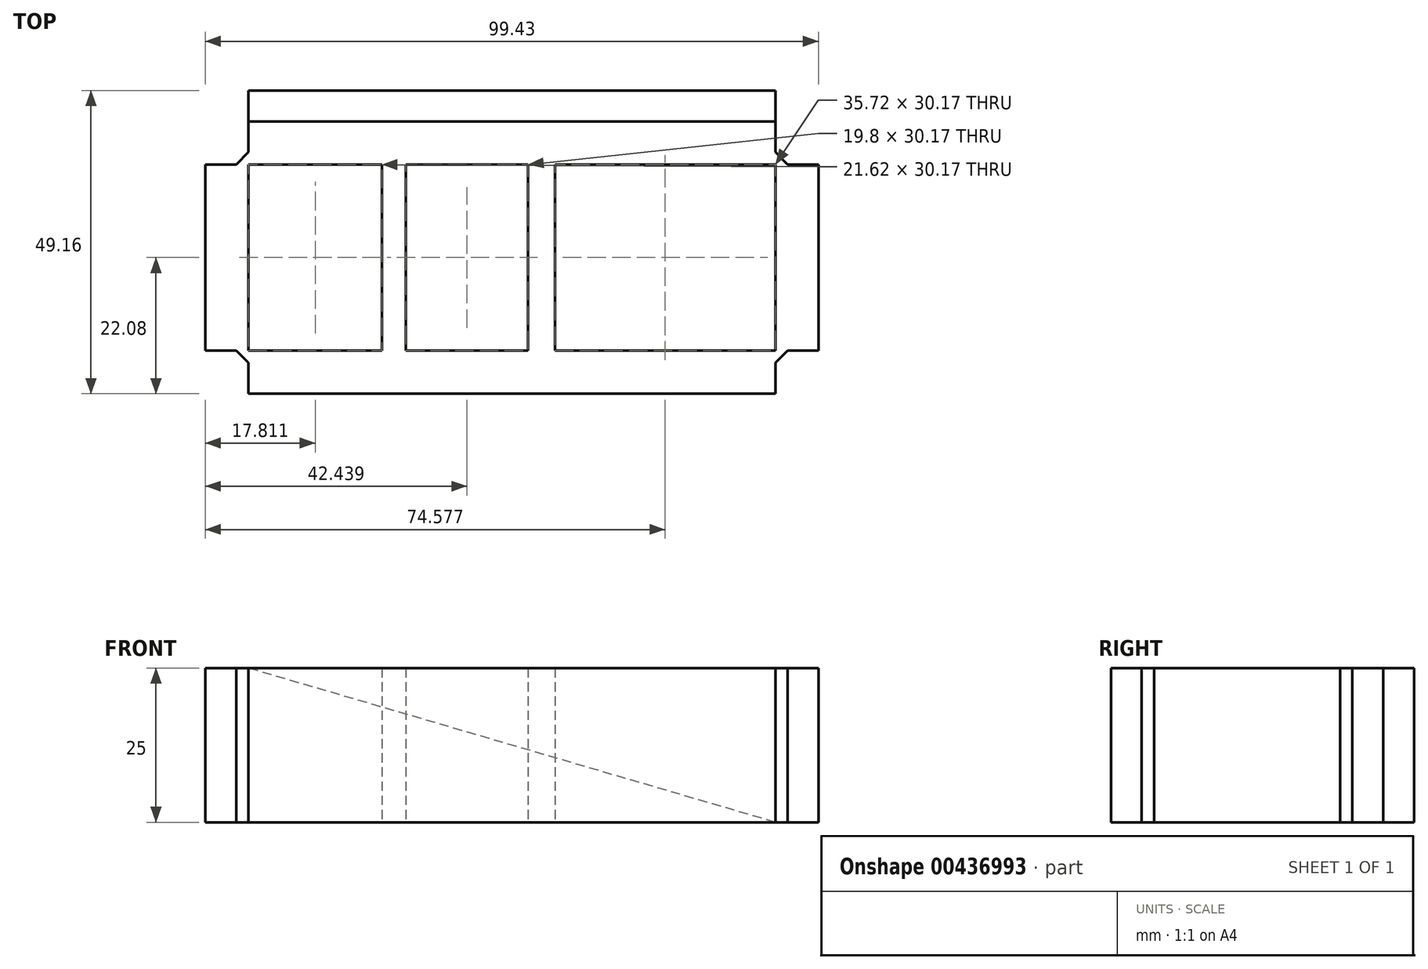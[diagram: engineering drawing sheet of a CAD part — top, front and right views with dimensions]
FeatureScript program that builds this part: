
annotation { "Feature Type Name" : "Feature", "Feature Type Description" : "" }
export const myFeature = defineFeature(function(context is Context, id is Id, definition is map)
    precondition{}
    {
        {
            var Q0;
            Q0=qCreatedBy(makeId("Top.planeOp"),FACE);
            var sketch = newSketch(context, id + "F0", { "sketchPlane" : qUnion([Q0])});
            skLineSegment(sketch, "E0.left", {"start": v(-36.76, 13.37) * mm, "end": v(-36.76, -16.8) * mm});
            skLineSegment(sketch, "E0.right", {"start": v(48.67, 13.37) * mm, "end": v(48.67, -16.8) * mm});
            skLineSegment(sketch, "E1.0", {"start": v(-38.76, 13.37) * mm, "end": v(-38.76, -16.8) * mm});
            skLineSegment(sketch, "E2.0", {"start": v(-36.76, 15.37) * mm, "end": v(48.67, 15.37) * mm});
            skLineSegment(sketch, "E3.0", {"start": v(50.67, 13.37) * mm, "end": v(50.67, -16.8) * mm});
            skLineSegment(sketch, "E4.0", {"start": v(-36.76, -18.8) * mm, "end": v(48.67, -18.8) * mm});
            skLineSegment(sketch, "E5", {"start": v(-36.76, 15.37) * mm, "end": v(-38.76, 13.37) * mm});
            skLineSegment(sketch, "E6", {"start": v(48.67, 15.37) * mm, "end": v(50.67, 13.37) * mm});
            skLineSegment(sketch, "E7", {"start": v(50.67, -16.8) * mm, "end": v(48.67, -18.8) * mm});
            skLineSegment(sketch, "E8", {"start": v(-36.76, -18.8) * mm, "end": v(-38.76, -16.8) * mm});
            skLineSegment(sketch, "E9", {"start": v(-15.14, 13.37) * mm, "end": v(-15.14, -16.8) * mm});
            skLineSegment(sketch, "E10", {"start": v(-11.22, 13.37) * mm, "end": v(-11.22, -16.8) * mm});
            skLineSegment(sketch, "E11", {"start": v(8.58, 13.37) * mm, "end": v(8.58, -16.8) * mm});
            skLineSegment(sketch, "E12", {"start": v(12.96, 13.37) * mm, "end": v(12.96, -16.8) * mm});
            skLineSegment(sketch, "E13", {"start": v(-36.76, 13.37) * mm, "end": v(-15.14, 13.37) * mm});
            skLineSegment(sketch, "E14", {"start": v(-11.22, 13.37) * mm, "end": v(8.58, 13.37) * mm});
            skLineSegment(sketch, "E15", {"start": v(48.67, 13.37) * mm, "end": v(12.96, 13.37) * mm});
            skLineSegment(sketch, "E16", {"start": v(-36.76, -16.8) * mm, "end": v(-15.14, -16.8) * mm});
            skLineSegment(sketch, "E17", {"start": v(-11.22, -16.8) * mm, "end": v(8.58, -16.8) * mm});
            skLineSegment(sketch, "E18", {"start": v(12.96, -16.8) * mm, "end": v(48.67, -16.8) * mm});
            skSolve(sketch);
        }
        {
            var Q0;
            Q0 = qSketchRegion(id + "F0", true);
            extrude(context, id + "F1", {"entities" : qUnion([Q0]), "depth" : 25 * mm});
        }
        {
            var Q0;
            Q0=makeQuery(id+"F1.opExtrude","SWEPT_FACE",FACE,{"disambiguationData":[OSD([sQuery(id+"F0.wireOp",EDGE,"E2.0")])]});
            var sketch = newSketch(context, id + "F2", { "sketchPlane" : qUnion([Q0])});
            skLineSegment(sketch, "E19.bottom", {"start": v(-48.67, 25) * mm, "end": v(36.76, 25) * mm});
            skLineSegment(sketch, "E19.top", {"start": v(-48.67, 0) * mm, "end": v(36.76, 0) * mm});
            skLineSegment(sketch, "E19.left", {"start": v(-48.67, 25) * mm, "end": v(-48.67, 0) * mm});
            skLineSegment(sketch, "E19.right", {"start": v(36.76, 25) * mm, "end": v(36.76, 0) * mm});
            skSolve(sketch);
        }
        {
            var Q0;
            Q0=makeQuery(id+"F2.imprint","IMPRINT",FACE,{"disambiguationData":[TD([[makeQuery(id+"F2.imprint","IMPRINT",EDGE,{"derivedFrom":sQuery(id+"F2.wireOp",EDGE,"E19.bottom")}),1.0]])]});
            extrude(context, id + "F3", {"entities" : qUnion([Q0]), "operationType" : NewBodyOperationType.ADD, "depth" : 5 * mm});
        }
        {
            var Q0;
            Q0=makeQuery(id+"F1.opExtrude","SWEPT_FACE",FACE,{"disambiguationData":[OSD([sQuery(id+"F0.wireOp",EDGE,"E4.0")])]});
            var sketch = newSketch(context, id + "F4", { "sketchPlane" : qUnion([Q0])});
            skLineSegment(sketch, "E20.bottom", {"start": v(-36.76, 25) * mm, "end": v(48.67, 25) * mm});
            skLineSegment(sketch, "E20.top", {"start": v(-36.76, 0) * mm, "end": v(48.67, 0) * mm});
            skLineSegment(sketch, "E20.left", {"start": v(-36.76, 25) * mm, "end": v(-36.76, 0) * mm});
            skLineSegment(sketch, "E20.right", {"start": v(48.67, 25) * mm, "end": v(48.67, 0) * mm});
            skSolve(sketch);
        }
        {
            var Q0;
            Q0=makeQuery(id+"F4.imprint","IMPRINT",FACE,{"disambiguationData":[TD([[makeQuery(id+"F4.imprint","IMPRINT",EDGE,{"derivedFrom":sQuery(id+"F4.wireOp",EDGE,"E20.bottom")}),-1.0]])]});
            extrude(context, id + "F5", {"entities" : qUnion([Q0]), "operationType" : NewBodyOperationType.ADD, "depth" : 5 * mm});
        }
        {
            var Q0;
            Q0=makeQuery(id+"F1.opExtrude","SWEPT_FACE",FACE,{"disambiguationData":[OSD([sQuery(id+"F0.wireOp",EDGE,"E1.0")])]});
            var sketch = newSketch(context, id + "F6", { "sketchPlane" : qUnion([Q0])});
            skLineSegment(sketch, "E21.bottom", {"start": v(-13.37, 25) * mm, "end": v(16.8, 25) * mm});
            skLineSegment(sketch, "E21.top", {"start": v(-13.37, 0) * mm, "end": v(16.8, 0) * mm});
            skLineSegment(sketch, "E21.left", {"start": v(-13.37, 25) * mm, "end": v(-13.37, 0) * mm});
            skLineSegment(sketch, "E21.right", {"start": v(16.8, 25) * mm, "end": v(16.8, 0) * mm});
            skSolve(sketch);
        }
        {
            var Q0;
            Q0=makeQuery(id+"F6.imprint","IMPRINT",FACE,{"disambiguationData":[TD([[makeQuery(id+"F6.imprint","IMPRINT",EDGE,{"derivedFrom":sQuery(id+"F6.wireOp",EDGE,"E21.bottom")}),-1.0]])]});
            extrude(context, id + "F7", {"entities" : qUnion([Q0]), "operationType" : NewBodyOperationType.ADD, "depth" : 5 * mm});
        }
        {
            var Q0;
            Q0=makeQuery(id+"F1.opExtrude","SWEPT_FACE",FACE,{"disambiguationData":[OSD([sQuery(id+"F0.wireOp",EDGE,"E3.0")])]});
            var sketch = newSketch(context, id + "F8", { "sketchPlane" : qUnion([Q0])});
            skLineSegment(sketch, "E22.bottom", {"start": v(-16.8, 25) * mm, "end": v(13.37, 25) * mm});
            skLineSegment(sketch, "E22.top", {"start": v(-16.8, 0) * mm, "end": v(13.37, 0) * mm});
            skLineSegment(sketch, "E22.left", {"start": v(-16.8, 25) * mm, "end": v(-16.8, 0) * mm});
            skLineSegment(sketch, "E22.right", {"start": v(13.37, 25) * mm, "end": v(13.37, 0) * mm});
            skSolve(sketch);
        }
        {
            var Q0;
            Q0=makeQuery(id+"F8.imprint","IMPRINT",FACE,{"disambiguationData":[TD([[makeQuery(id+"F8.imprint","IMPRINT",EDGE,{"derivedFrom":sQuery(id+"F8.wireOp",EDGE,"E22.bottom")}),1.0]])]});
            extrude(context, id + "F9", {"entities" : qUnion([Q0]), "operationType" : NewBodyOperationType.ADD, "depth" : 5 * mm});
        }
        {
            var Q0;
            Q0=makeQuery(id+"F3.opExtrude","CAP_FACE",FACE,{"disambiguationData":[OSD([sQuery(id+"F2.wireOp",EDGE,"E19.bottom"),sQuery(id+"F2.wireOp",EDGE,"E19.top"),sQuery(id+"F2.wireOp",EDGE,"E19.left"),sQuery(id+"F2.wireOp",EDGE,"E19.right")])],"isStart":false});
            var sketch = newSketch(context, id + "F10", { "sketchPlane" : qUnion([Q0])});
            skLineSegment(sketch, "E23", {"start": v(-48.67, 0) * mm, "end": v(36.76, 25) * mm});
            skLineSegment(sketch, "E24", {"start": v(36.76, 25) * mm, "end": v(36.76, 0) * mm});
            skLineSegment(sketch, "E25", {"start": v(36.76, 0) * mm, "end": v(-48.67, 0) * mm});
            skSolve(sketch);
        }
        {
            var Q0;
            Q0=makeQuery(id+"F10.imprint","IMPRINT",FACE,{"disambiguationData":[TD([[makeQuery(id+"F10.imprint","IMPRINT",EDGE,{"derivedFrom":sQuery(id+"F10.wireOp",EDGE,"E23")}),-1.0]])]});
            extrude(context, id + "F11", {"entities" : qUnion([Q0]), "operationType" : NewBodyOperationType.ADD, "depth" : 5 * mm});
        }
    });
